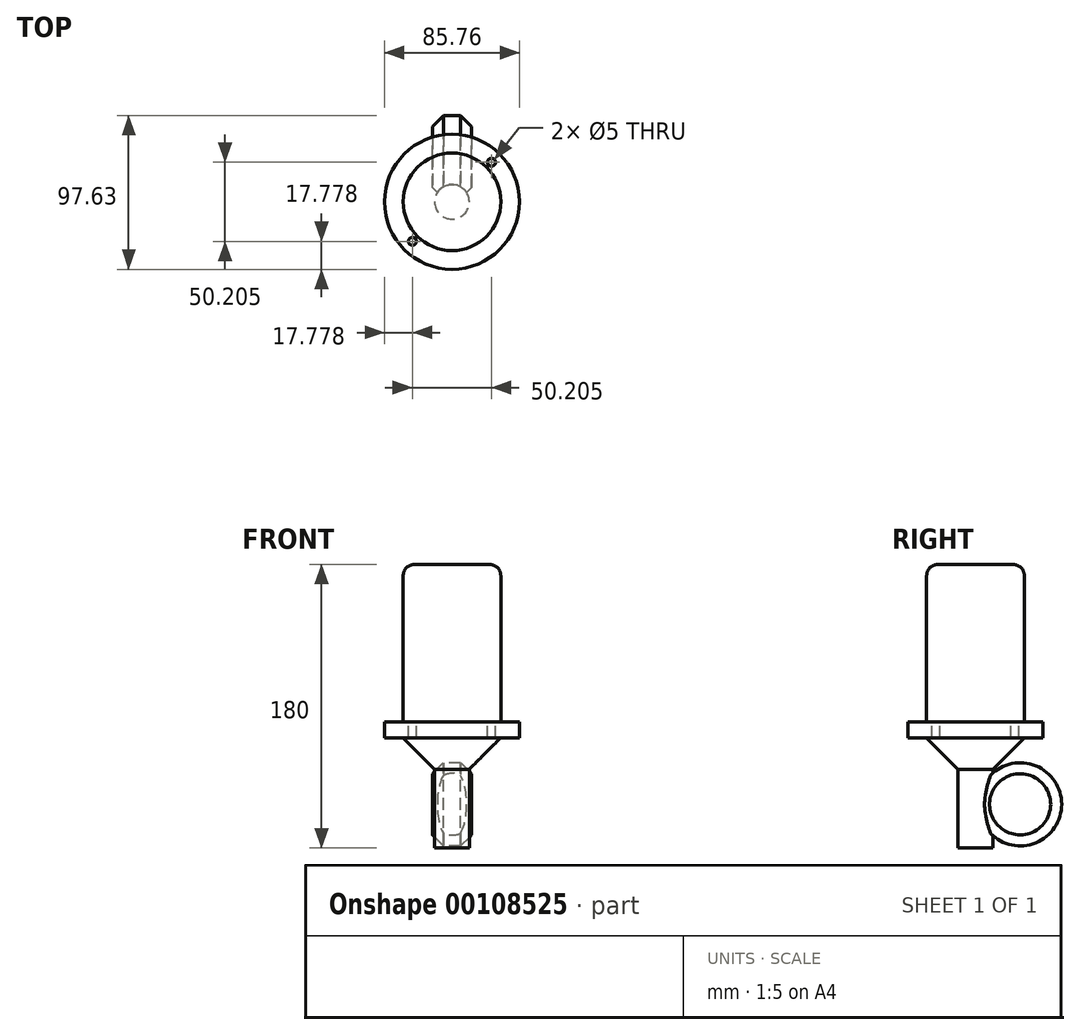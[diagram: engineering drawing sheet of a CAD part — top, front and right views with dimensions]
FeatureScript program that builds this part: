
annotation { "Feature Type Name" : "Feature", "Feature Type Description" : "" }
export const myFeature = defineFeature(function(context is Context, id is Id, definition is map)
    precondition{}
    {
        {
            var Q0;
            Q0=qCreatedBy(makeId("Top.planeOp"),FACE);
            var sketch = newSketch(context, id + "F0", { "sketchPlane" : qUnion([Q0])});
            skCircle(sketch, "E0", {"center": v(0, 0) * mm, "radius": 31 * mm});
            skLineSegment(sketch, "E1", {"start": v(0, 0) * mm, "end": v(25.1, 25.1) * mm, "construction": true});
            skCircle(sketch, "E2", {"center": v(25.1, 25.1) * mm, "radius": 2.5 * mm});
            skLineSegment(sketch, "E3", {"start": v(0, 0) * mm, "end": v(-25.1, -25.1) * mm, "construction": true});
            skCircle(sketch, "E4", {"center": v(-25.1, -25.1) * mm, "radius": 2.5 * mm});
            skCircle(sketch, "E5", {"center": v(0, 0) * mm, "radius": 42.88 * mm});
            skCircle(sketch, "E6", {"center": v(0, 0) * mm, "radius": 11.08 * mm});
            skLineSegment(sketch, "E7", {"start": v(0, 0) * mm, "end": v(28.59, 0) * mm, "construction": true});
            skSolve(sketch);
        }
        {
            var Q0;
            Q0=makeQuery(id+"F0.imprint","IMPRINT",FACE,{"disambiguationData":[TD([[makeQuery(id+"F0.imprint","IMPRINT",EDGE,{"derivedFrom":sQuery(id+"F0.wireOp",EDGE,"E0")}),1.0]])]});
            var Q1;
            Q1=makeQuery(id+"F0.imprint","IMPRINT",FACE,{"disambiguationData":[TD([[makeQuery(id+"F0.imprint","IMPRINT",EDGE,{"derivedFrom":sQuery(id+"F0.wireOp",EDGE,"E6")}),1.0]])]});
            extrude(context, id + "F1", {"entities" : qUnion([Q0, Q1]), "depth" : 100 * mm});
        }
        {
            var Q0;
            Q0=makeQuery(id+"F1.opExtrude","CAP_EDGE",EDGE,{"disambiguationData":[OSD([sQuery(id+"F0.wireOp",EDGE,"E0")])],"isStart":false});
            fillet(context, id + "F2", {"entities" : qUnion([Q0]), "radius" : 7 * mm, "tangentPropagation" : true, "allowEdgeOverflow" : false});
        }
        {
            var Q0;
            Q0=qSketchRegion(id+"F0",true);
            extrude(context, id + "F3", {"entities" : qUnion([Q0]), "operationType" : NewBodyOperationType.ADD, "oppositeDirection" : true, "depth" : 10 * mm});
        }
        {
            var Q0;
            Q0=makeQuery(id+"F0.imprint","IMPRINT",FACE,{"disambiguationData":[TD([[makeQuery(id+"F0.imprint","IMPRINT",EDGE,{"derivedFrom":sQuery(id+"F0.wireOp",EDGE,"E6")}),1.0]])]});
            extrude(context, id + "F4", {"entities" : qUnion([Q0]), "operationType" : NewBodyOperationType.ADD, "oppositeDirection" : true, "depth" : 30 * mm});
        }
        {
            var Q0;
            Q0=makeQuery(id+"F0.imprint","IMPRINT",FACE,{"disambiguationData":[TD([[makeQuery(id+"F0.imprint","IMPRINT",EDGE,{"derivedFrom":sQuery(id+"F0.wireOp",EDGE,"E0")}),1.0]])]});
            extrude(context, id + "F5", {"entities" : qUnion([Q0]), "operationType" : NewBodyOperationType.ADD, "oppositeDirection" : true, "depth" : 30 * mm});
        }
        {
            var Q0;
            Q0=makeQuery(id+"F5.opExtrude","CAP_EDGE",EDGE,{"disambiguationData":[OSD([sQuery(id+"F0.wireOp",EDGE,"E0")])],"isStart":false});
            chamfer(context, id + "F6", {"entities" : qUnion([Q0]), "width" : 20 * mm, "tangentPropagation" : true});
        }
        {
            var Q0;
            {var subQ0=sQuery(id+"F0.wireOp",EDGE,"E6");Q0=makeQuery(id+"F5.boolean.opBoolean","MERGE",FACE,{"derivedFrom":[makeQuery(id+"F4.opExtrude","CAP_FACE",FACE,{"disambiguationData":[OSD([subQ0])],"isStart":false}),makeQuery(id+"F5.opExtrude","CAP_FACE",FACE,{"disambiguationData":[OSD([sQuery(id+"F0.wireOp",EDGE,"E0"),subQ0])],"isStart":false})]});}
            extrude(context, id + "F7", {"entities" : qUnion([Q0]), "operationType" : NewBodyOperationType.ADD, "depth" : 50 * mm});
        }
        {
            var Q0;
            Q0=qCreatedBy(makeId("Right.planeOp"),FACE);
            var sketch = newSketch(context, id + "F8", { "sketchPlane" : qUnion([Q0])});
            skCircle(sketch, "E8", {"center": v(28.36, -52.31) * mm, "radius": 26.4 * mm});
            skSolve(sketch);
        }
        {
            var Q0;
            Q0=makeQuery(id+"F8.imprint","IMPRINT",FACE,{"disambiguationData":[TD([[makeQuery(id+"F8.imprint","IMPRINT",EDGE,{"derivedFrom":sQuery(id+"F8.wireOp",EDGE,"E8")}),1.0]])]});
            extrude(context, id + "F9", {"entities" : qUnion([Q0]), "operationType" : NewBodyOperationType.ADD, "endBound" : BoundingType.SYMMETRIC, "depth" : 25 * mm});
        }
        {
            var Q0;
            Q0=makeQuery(id+"F9.opExtrude","CAP_EDGE",EDGE,{"disambiguationData":[OSD([sQuery(id+"F8.wireOp",EDGE,"E8")])],"isStart":false});
            var Q1;
            Q1=makeQuery(id+"F9.opExtrude","CAP_EDGE",EDGE,{"disambiguationData":[OSD([sQuery(id+"F8.wireOp",EDGE,"E8")])],"isStart":true});
            chamfer(context, id + "F10", {"entities" : qUnion([Q0, Q1]), "width" : 7 * mm, "tangentPropagation" : true});
        }
    });
